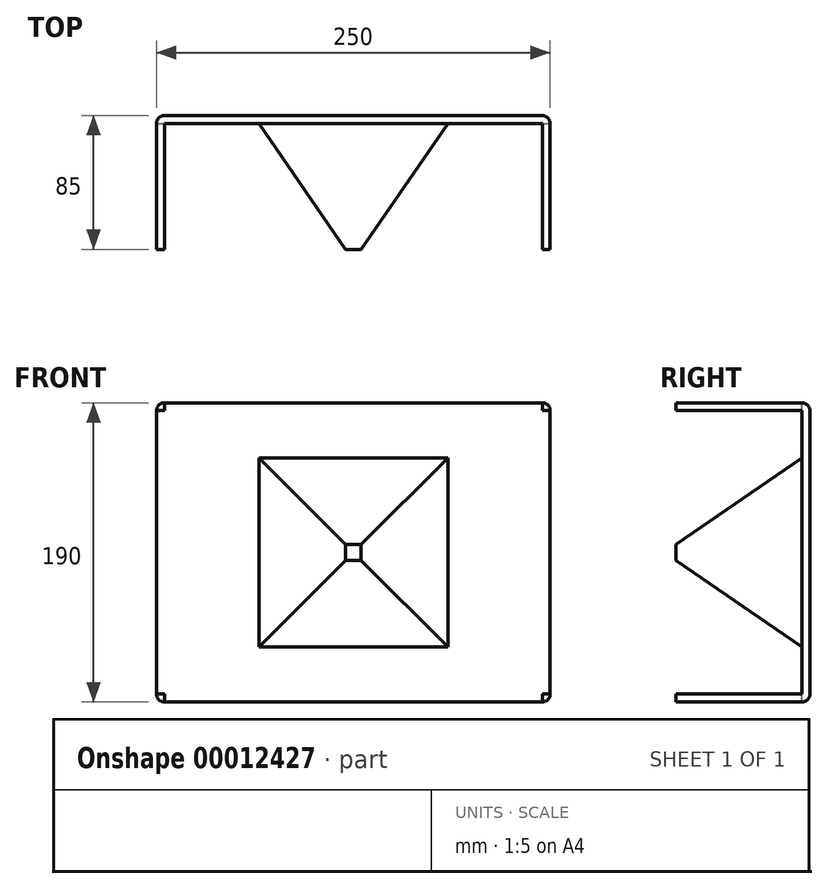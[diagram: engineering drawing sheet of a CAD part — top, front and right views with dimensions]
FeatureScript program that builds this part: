
annotation { "Feature Type Name" : "Feature", "Feature Type Description" : "" }
export const myFeature = defineFeature(function(context is Context, id is Id, definition is map)
    precondition{}
    {
        {
            var Q0;
            Q0=qCreatedBy(makeId("Front.planeOp"),FACE);
            cPlane(context, id + "F0", {"entities" : qUnion([Q0]), "cplaneType" : CPlaneType.OFFSET, "offset" : 75 * mm, "width" : 150 * mm, "height" : 150 * mm});
        }
        {
            var Q0;
            Q0=qCreatedBy(id+"F0.planeOp",FACE);
            var sketch = newSketch(context, id + "F1", { "sketchPlane" : qUnion([Q0])});
            skLineSegment(sketch, "E0.rect.bottom", {"start": v(125, -95) * mm, "end": v(-125, -95) * mm});
            skLineSegment(sketch, "E0.rect.top", {"start": v(125, 95) * mm, "end": v(-125, 95) * mm});
            skLineSegment(sketch, "E0.rect.left", {"start": v(125, -95) * mm, "end": v(125, 95) * mm});
            skLineSegment(sketch, "E0.rect.right", {"start": v(-125, -95) * mm, "end": v(-125, 95) * mm});
            skPoint(sketch, "E0.rect.middle", {"position": v(0, 0) * mm});
            skSolve(sketch);
        }
        {
            var Q0;
            Q0=makeQuery(id+"F1.imprint","IMPRINT",FACE,{"disambiguationData":[TD([[makeQuery(id+"F1.imprint","IMPRINT",EDGE,{"derivedFrom":sQuery(id+"F1.wireOp",EDGE,"E0.rect.bottom")}),-1.0]])]});
            extrude(context, id + "F2", {"entities" : qUnion([Q0]), "oppositeDirection" : true, "depth" : 90 * mm});
        }
        {
            var Q0;
            Q0=makeQuery(id+"F2.opExtrude","SWEPT_FACE",FACE,{"disambiguationData":[OSD([sQuery(id+"F1.wireOp",EDGE,"E0.rect.top")])]});
            var Q1;
            Q1=makeQuery(id+"F2.opExtrude","CAP_FACE",FACE,{"disambiguationData":[OSD([sQuery(id+"F1.wireOp",EDGE,"E0.rect.bottom"),sQuery(id+"F1.wireOp",EDGE,"E0.rect.top"),sQuery(id+"F1.wireOp",EDGE,"E0.rect.left"),sQuery(id+"F1.wireOp",EDGE,"E0.rect.right")])],"isStart":false});
            var Q2;
            Q2=makeQuery(id+"F2.opExtrude","SWEPT_FACE",FACE,{"disambiguationData":[OSD([sQuery(id+"F1.wireOp",EDGE,"E0.rect.left")])]});
            var Q3;
            Q3=makeQuery(id+"F2.opExtrude","CAP_EDGE",EDGE,{"disambiguationData":[OSD([sQuery(id+"F1.wireOp",EDGE,"E0.rect.top")])],"isStart":true});
            var Q4;
            Q4=makeQuery(id+"F2.opExtrude","CAP_FACE",FACE,{"disambiguationData":[OSD([sQuery(id+"F1.wireOp",EDGE,"E0.rect.bottom"),sQuery(id+"F1.wireOp",EDGE,"E0.rect.top"),sQuery(id+"F1.wireOp",EDGE,"E0.rect.left"),sQuery(id+"F1.wireOp",EDGE,"E0.rect.right")])],"isStart":true});
            var Q5;
            Q5=makeQuery(id+"F2.opExtrude","SWEPT_FACE",FACE,{"disambiguationData":[OSD([sQuery(id+"F1.wireOp",EDGE,"E0.rect.bottom")])]});
            fillet(context, id + "F3", {"entities" : qUnion([Q0, Q1, Q2, Q3, Q4, Q5]), "radius" : 5 * mm, "tangentPropagation" : true, "allowEdgeOverflow" : false});
        }
        {
            var Q0;
            Q0=makeQuery(id+"F2.opExtrude","SWEPT_FACE",FACE,{"disambiguationData":[OSD([sQuery(id+"F1.wireOp",EDGE,"E0.rect.top")])]});
            var sketch = newSketch(context, id + "F4", { "sketchPlane" : qUnion([Q0])});
            skLineSegment(sketch, "E1", {"start": v(-60, 10) * mm, "end": v(0, 10) * mm});
            skLineSegment(sketch, "E2", {"start": v(0, 10) * mm, "end": v(60, 10) * mm});
            skLineSegment(sketch, "E3", {"start": v(60, 10) * mm, "end": v(5, -70) * mm});
            skLineSegment(sketch, "E4", {"start": v(5, -70) * mm, "end": v(0, -70) * mm});
            skLineSegment(sketch, "E5", {"start": v(0, -70) * mm, "end": v(-5, -70) * mm});
            skLineSegment(sketch, "E6", {"start": v(-5, -70) * mm, "end": v(-60, 10) * mm});
            skSolve(sketch);
        }
        {
            var Q0;
            Q0=makeQuery(id+"F2.opExtrude","SWEPT_FACE",FACE,{"disambiguationData":[OSD([sQuery(id+"F1.wireOp",EDGE,"E0.rect.left")])]});
            var sketch = newSketch(context, id + "F5", { "sketchPlane" : qUnion([Q0])});
            skLineSegment(sketch, "E7", {"start": v(10, 60) * mm, "end": v(10, 0) * mm});
            skLineSegment(sketch, "E8", {"start": v(10, 0) * mm, "end": v(10, -60) * mm});
            skLineSegment(sketch, "E9", {"start": v(10, -60) * mm, "end": v(-70, -5) * mm});
            skLineSegment(sketch, "E10", {"start": v(-70, -5) * mm, "end": v(-70, 0) * mm});
            skLineSegment(sketch, "E11", {"start": v(-70, 0) * mm, "end": v(-70, 5) * mm});
            skLineSegment(sketch, "E12", {"start": v(-70, 5) * mm, "end": v(10, 60) * mm});
            skSolve(sketch);
        }
        {
            var Q0;
            {var subQ3=sQuery(id+"F4.wireOp",EDGE,"E3");Q0=makeQuery(id+"F4.imprint","IMPRINT",FACE,{"disambiguationData":[TD([[makeQuery(id+"F4.imprint","IMPRINT",EDGE,{"derivedFrom":subQ3}),1.0]])]});}
            var Q1;
            {var subQ3=sQuery(id+"F4.wireOp",EDGE,"E6");Q1=makeQuery(id+"F4.imprint","IMPRINT",FACE,{"disambiguationData":[TD([[makeQuery(id+"F4.imprint","IMPRINT",EDGE,{"derivedFrom":subQ3}),1.0]])]});}
            extrude(context, id + "F6", {"entities" : qUnion([Q0, Q1]), "operationType" : NewBodyOperationType.REMOVE, "oppositeDirection" : true, "depth" : 250 * mm});
        }
        {
            var Q0;
            {var subQ3=sQuery(id+"F5.wireOp",EDGE,"E12");Q0=makeQuery(id+"F5.imprint","IMPRINT",FACE,{"disambiguationData":[TD([[makeQuery(id+"F5.imprint","IMPRINT",EDGE,{"derivedFrom":subQ3}),1.0]])]});}
            var Q1;
            {var subQ3=sQuery(id+"F5.wireOp",EDGE,"E9");Q1=makeQuery(id+"F5.imprint","IMPRINT",FACE,{"disambiguationData":[TD([[makeQuery(id+"F5.imprint","IMPRINT",EDGE,{"derivedFrom":subQ3}),1.0]])]});}
            extrude(context, id + "F7", {"entities" : qUnion([Q0, Q1]), "operationType" : NewBodyOperationType.REMOVE, "oppositeDirection" : true, "depth" : 250 * mm});
        }
        {
            var Q0;
            Q0=makeQuery(id+"F2.opExtrude","SWEPT_FACE",FACE,{"disambiguationData":[OSD([sQuery(id+"F1.wireOp",EDGE,"E0.rect.left")])]});
            extrude(context, id + "F8", {"entities" : qUnion([Q0]), "operationType" : NewBodyOperationType.REMOVE, "oppositeDirection" : true, "depth" : 5 * mm});
        }
        {
            var Q0;
            Q0=makeQuery(id+"F2.opExtrude","SWEPT_FACE",FACE,{"disambiguationData":[OSD([sQuery(id+"F1.wireOp",EDGE,"E0.rect.bottom")])]});
            extrude(context, id + "F9", {"entities" : qUnion([Q0]), "operationType" : NewBodyOperationType.REMOVE, "oppositeDirection" : true, "depth" : 5 * mm});
        }
        {
            var Q0;
            Q0=makeQuery(id+"F2.opExtrude","SWEPT_FACE",FACE,{"disambiguationData":[OSD([sQuery(id+"F1.wireOp",EDGE,"E0.rect.right")])]});
            extrude(context, id + "F10", {"entities" : qUnion([Q0]), "operationType" : NewBodyOperationType.REMOVE, "oppositeDirection" : true, "depth" : 5 * mm});
        }
        {
            var Q0;
            Q0=makeQuery(id+"F2.opExtrude","SWEPT_FACE",FACE,{"disambiguationData":[OSD([sQuery(id+"F1.wireOp",EDGE,"E0.rect.top")])]});
            extrude(context, id + "F11", {"entities" : qUnion([Q0]), "operationType" : NewBodyOperationType.REMOVE, "oppositeDirection" : true, "depth" : 5 * mm});
        }
        {
            var Q0;
            Q0=makeQuery(id+"F1.imprint","IMPRINT",FACE,{"disambiguationData":[TD([[makeQuery(id+"F1.imprint","IMPRINT",EDGE,{"derivedFrom":sQuery(id+"F1.wireOp",EDGE,"E0.rect.bottom")}),-1.0]])]});
            extrude(context, id + "F12", {"entities" : qUnion([Q0]), "operationType" : NewBodyOperationType.REMOVE, "oppositeDirection" : true, "depth" : 5 * mm});
        }
    });
